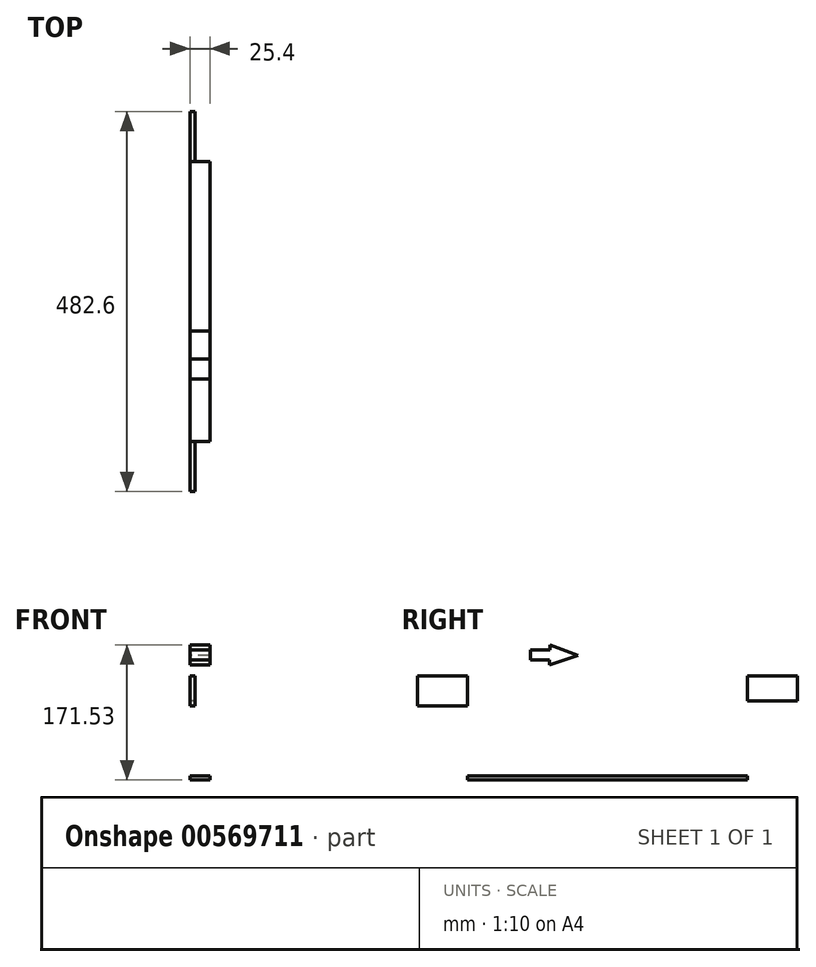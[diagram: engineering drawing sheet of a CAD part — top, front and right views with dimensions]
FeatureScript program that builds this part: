
annotation { "Feature Type Name" : "Feature", "Feature Type Description" : "" }
export const myFeature = defineFeature(function(context is Context, id is Id, definition is map)
    precondition{}
    {
        {
            var Q0;
            Q0=qCreatedBy(makeId("Right.planeOp"),FACE);
            var sketch = newSketch(context, id + "F0", { "sketchPlane" : qUnion([Q0])});
            skLineSegment(sketch, "E0.bottom", {"start": v(-107.28, -57.57) * mm, "end": v(248.32, -57.57) * mm});
            skLineSegment(sketch, "E0.top", {"start": v(-107.28, -62.65) * mm, "end": v(248.32, -62.65) * mm});
            skLineSegment(sketch, "E0.left", {"start": v(-107.28, -57.57) * mm, "end": v(-107.28, -62.65) * mm});
            skLineSegment(sketch, "E0.right", {"start": v(248.32, -57.57) * mm, "end": v(248.32, -62.65) * mm});
            skLineSegment(sketch, "E1.bottom", {"start": v(-107.28, -57.57) * mm, "end": v(-100.93, -57.57) * mm});
            skLineSegment(sketch, "E1.top", {"start": v(-107.28, 69.43) * mm, "end": v(-100.93, 69.43) * mm});
            skLineSegment(sketch, "E1.left", {"start": v(-107.28, -57.57) * mm, "end": v(-107.28, 69.43) * mm});
            skLineSegment(sketch, "E1.right", {"start": v(-100.93, -57.57) * mm, "end": v(-100.93, 69.43) * mm});
            skLineSegment(sketch, "E2.bottom", {"start": v(248.32, -57.57) * mm, "end": v(241.97, -57.57) * mm});
            skLineSegment(sketch, "E2.top", {"start": v(248.32, 69.43) * mm, "end": v(241.97, 69.43) * mm});
            skLineSegment(sketch, "E2.left", {"start": v(248.32, -57.57) * mm, "end": v(248.32, 69.43) * mm});
            skLineSegment(sketch, "E2.right", {"start": v(241.97, -57.57) * mm, "end": v(241.97, 69.43) * mm});
            skLineSegment(sketch, "E3.bottom", {"start": v(248.32, 69.43) * mm, "end": v(311.82, 69.43) * mm});
            skLineSegment(sketch, "E3.top", {"start": v(248.32, 37.83) * mm, "end": v(311.82, 37.83) * mm});
            skLineSegment(sketch, "E3.left", {"start": v(248.32, 69.43) * mm, "end": v(248.32, 37.83) * mm});
            skLineSegment(sketch, "E3.right", {"start": v(311.82, 69.43) * mm, "end": v(311.82, 37.83) * mm});
            skLineSegment(sketch, "E4.bottom", {"start": v(-107.28, 69.43) * mm, "end": v(-170.78, 69.43) * mm});
            skLineSegment(sketch, "E4.top", {"start": v(-107.28, 31.33) * mm, "end": v(-170.78, 31.33) * mm});
            skLineSegment(sketch, "E4.left", {"start": v(-107.28, 69.43) * mm, "end": v(-107.28, 31.33) * mm});
            skLineSegment(sketch, "E4.right", {"start": v(-170.78, 69.43) * mm, "end": v(-170.78, 31.33) * mm});
            skLineSegment(sketch, "E5", {"start": v(-2.65, 108.88) * mm, "end": v(33.1, 95.66) * mm});
            skLineSegment(sketch, "E6", {"start": v(33.1, 95.66) * mm, "end": v(-3, 83.48) * mm});
            skLineSegment(sketch, "E7", {"start": v(-3, 83.48) * mm, "end": v(-3, 89.83) * mm});
            skLineSegment(sketch, "E8", {"start": v(-3, 89.83) * mm, "end": v(-27.62, 89.83) * mm});
            skLineSegment(sketch, "E9", {"start": v(-27.62, 89.83) * mm, "end": v(-27.62, 102.53) * mm});
            skLineSegment(sketch, "E10", {"start": v(-27.62, 102.53) * mm, "end": v(-2.65, 102.53) * mm});
            skLineSegment(sketch, "E11", {"start": v(-2.65, 102.53) * mm, "end": v(-2.65, 108.88) * mm});
            skSolve(sketch);
        }
        {
            var Q0;
            Q0=makeQuery(id+"F0.imprint","IMPRINT",FACE,{"disambiguationData":[TD([[makeQuery(id+"F0.imprint","IMPRINT",EDGE,{"derivedFrom":sQuery(id+"F0.wireOp",EDGE,"E2.bottom")}),-1.0]])]});
            var Q1;
            Q1=makeQuery(id+"F0.imprint","IMPRINT",FACE,{"disambiguationData":[TD([[makeQuery(id+"F0.imprint","IMPRINT",EDGE,{"derivedFrom":sQuery(id+"F0.wireOp",EDGE,"E0.bottom")}),-1.0]])]});
            var Q2;
            Q2=makeQuery(id+"F0.imprint","IMPRINT",FACE,{"disambiguationData":[TD([[makeQuery(id+"F0.imprint","IMPRINT",EDGE,{"derivedFrom":sQuery(id+"F0.wireOp",EDGE,"E1.bottom")}),1.0]])]});
            extrude(context, id + "F1", {"entities" : qUnion([Q0, Q1, Q2]), "depth" : 25.4 * mm, "offsetDistance" : 25.4 * mm});
        }
        {
            var Q0;
            Q0=makeQuery(id+"F0.imprint","IMPRINT",FACE,{"disambiguationData":[TD([[makeQuery(id+"F0.imprint","IMPRINT",EDGE,{"derivedFrom":sQuery(id+"F0.wireOp",EDGE,"E3.bottom")}),-1.0]])]});
            extrude(context, id + "F2", {"entities" : qUnion([Q0]), "depth" : 6.35 * mm, "offsetDistance" : 25.4 * mm});
        }
        {
            var Q0;
            Q0=makeQuery(id+"F0.imprint","IMPRINT",FACE,{"disambiguationData":[TD([[makeQuery(id+"F0.imprint","IMPRINT",EDGE,{"derivedFrom":sQuery(id+"F0.wireOp",EDGE,"E4.bottom")}),1.0]])]});
            extrude(context, id + "F3", {"entities" : qUnion([Q0]), "depth" : 6.35 * mm, "offsetDistance" : 25.4 * mm});
        }
        {
            var Q0;
            Q0=makeQuery(id+"F0.imprint","IMPRINT",FACE,{"disambiguationData":[TD([[makeQuery(id+"F0.imprint","IMPRINT",EDGE,{"derivedFrom":sQuery(id+"F0.wireOp",EDGE,"E5")}),-1.0]])]});
            extrude(context, id + "F4", {"entities" : qUnion([Q0]), "depth" : 25.4 * mm, "offsetDistance" : 25.4 * mm});
        }
    });
